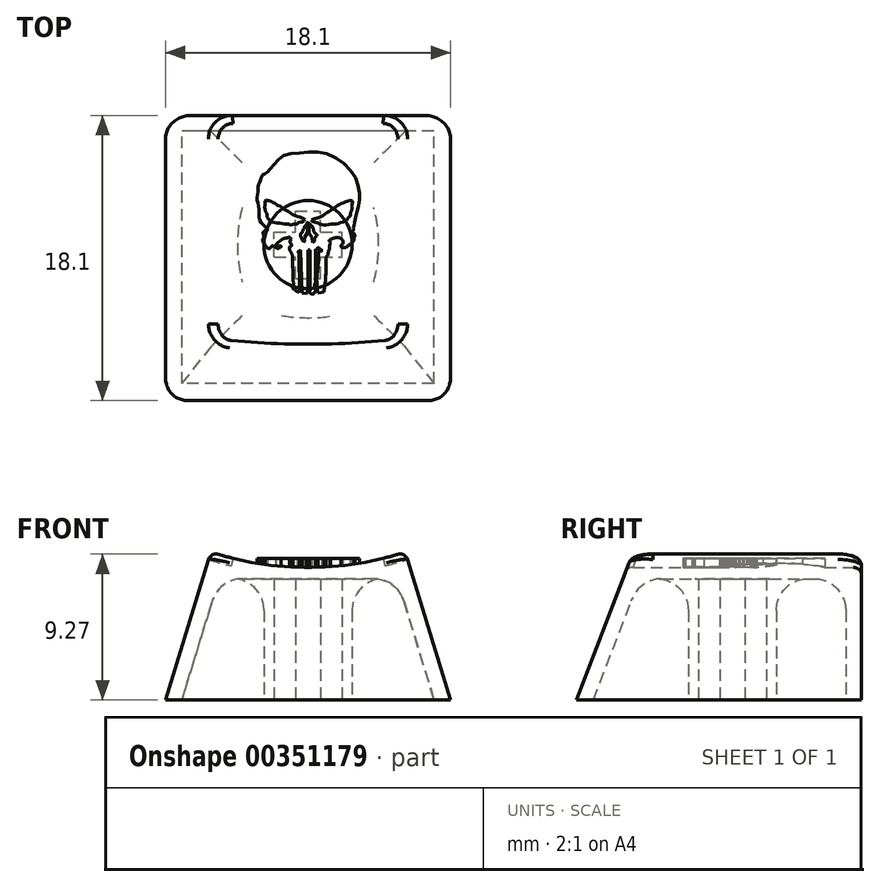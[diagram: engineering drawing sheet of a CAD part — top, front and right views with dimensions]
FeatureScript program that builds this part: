
annotation { "Feature Type Name" : "Feature", "Feature Type Description" : "" }
export const myFeature = defineFeature(function(context is Context, id is Id, definition is map)
    precondition{}
    {
        {
            var Q0;
            Q0=qCreatedBy(makeId("Front.planeOp"),FACE);
            var sketch = newSketch(context, id + "F0", { "sketchPlane" : qUnion([Q0])});
            skLineSegment(sketch, "E0", {"start": v(-8, 0) * mm, "end": v(-5.66, 7.7) * mm});
            skLineSegment(sketch, "E1", {"start": v(-5.66, 7.7) * mm, "end": v(5.66, 7.7) * mm});
            skLineSegment(sketch, "E2", {"start": v(5.66, 7.7) * mm, "end": v(8, 0) * mm});
            skLineSegment(sketch, "E3", {"start": v(8, 0) * mm, "end": v(9.05, 0) * mm});
            skLineSegment(sketch, "E4", {"start": v(9.05, 0) * mm, "end": v(6.18, 9.4) * mm});
            skLineSegment(sketch, "E5", {"start": v(-6.19, 9.4) * mm, "end": v(-9.05, 0) * mm});
            skLineSegment(sketch, "E6", {"start": v(-9.05, 0) * mm, "end": v(-8, 0) * mm});
            skArc(sketch, "E7", {"start": v(-6.18, 9.4) * mm, "mid": v(0, 8.42) * mm, "end": v(6.18, 9.4) * mm});
            skSolve(sketch);
        }
        {
            var Q0;
            Q0 = qSketchRegion(id + "F0", true);
            extrude(context, id + "F1", {"entities" : qUnion([Q0]), "depth" : 4.2 * mm, "hasSecondDirection" : true, "secondDirectionOppositeDirection" : true, "secondDirectionDepth" : 8.2 * mm});
        }
        {
            var Q0;
            Q0=qCreatedBy(makeId("Right.planeOp"),FACE);
            var sketch = newSketch(context, id + "F2", { "sketchPlane" : qUnion([Q0])});
            skLineSegment(sketch, "E8.0.0", {"start": v(8.2, 0) * mm, "end": v(8.2, 7.7) * mm});
            skLineSegment(sketch, "E8.0.1", {"start": v(8.2, 7.7) * mm, "end": v(-4.2, 7.7) * mm});
            skLineSegment(sketch, "E8.0.2", {"start": v(-4.2, 7.7) * mm, "end": v(-4.2, 0) * mm});
            skLineSegment(sketch, "E8.0.3", {"start": v(-4.2, 0) * mm, "end": v(8.2, 0) * mm});
            skLineSegment(sketch, "E9", {"start": v(7.2, 7.7) * mm, "end": v(7.2, 0) * mm});
            skLineSegment(sketch, "E10", {"start": v(7.2, 0) * mm, "end": v(8.2, 0) * mm});
            skLineSegment(sketch, "E11", {"start": v(-6.67, 8.42) * mm, "end": v(-9.9, 0) * mm});
            skLineSegment(sketch, "E12", {"start": v(-9.9, 0) * mm, "end": v(-8.83, 0) * mm});
            skLineSegment(sketch, "E13", {"start": v(-8.83, 0) * mm, "end": v(-5.87, 7.7) * mm});
            skLineSegment(sketch, "E14", {"start": v(-4.2, 7.7) * mm, "end": v(-5.87, 7.7) * mm});
            skLineSegment(sketch, "E15", {"start": v(-4.2, 9.4) * mm, "end": v(-4.2, 7.7) * mm});
            skLineSegment(sketch, "E16.0.0", {"start": v(-4.2, 9.4) * mm, "end": v(-4.2, 8.42) * mm});
            skLineSegment(sketch, "E16.0.1", {"start": v(-4.2, 9.4) * mm, "end": v(-4.2, 0) * mm});
            skLineSegment(sketch, "E16.0.3", {"start": v(-4.2, 0) * mm, "end": v(-4.2, 7.7) * mm});
            skLineSegment(sketch, "E16.0.7", {"start": v(-4.2, 0) * mm, "end": v(-4.2, 9.4) * mm});
            skLineSegment(sketch, "E17", {"start": v(8.2, 8.42) * mm, "end": v(-4.2, 8.42) * mm});
            skLineSegment(sketch, "E18", {"start": v(-4.2, 8.42) * mm, "end": v(-6.67, 8.42) * mm});
            skSolve(sketch);
        }
        {
            var Q0;
            Q0=makeQuery(id+"F2.imprint","IMPRINT",FACE,{"disambiguationData":[TD([[makeQuery(id+"F2.imprint","IMPRINT",EDGE,{"derivedFrom":sQuery(id+"F2.wireOp",EDGE,"E11")}),1.0]])]});
            var Q1;
            {var subQ0=sQuery(id+"F2.wireOp",EDGE,"E14");Q1=makeQuery(id+"F2.imprint","IMPRINT",FACE,{"disambiguationData":[TD([[makeQuery(id+"F2.imprint","IMPRINT",EDGE,{"derivedFrom":subQ0}),1.0]])]});}
            var Q2;
            {var subQ0=sQuery(id+"F2.wireOp",EDGE,"E8.0.0");Q2=makeQuery(id+"F2.imprint","IMPRINT",FACE,{"disambiguationData":[TD([[makeQuery(id+"F2.imprint","IMPRINT",EDGE,{"derivedFrom":subQ0}),1.0]])]});}
            var Q3;
            Q3=makeQuery(id+"F1.opExtrude","SWEPT_FACE",FACE,{"disambiguationData":[OSD([sQuery(id+"F0.wireOp",EDGE,"E4")])]});
            var Q4;
            Q4=makeQuery(id+"F1.opExtrude","SWEPT_FACE",FACE,{"disambiguationData":[OSD([sQuery(id+"F0.wireOp",EDGE,"E5")])]});
            extrude(context, id + "F3", {"entities" : qUnion([Q0, Q1, Q2]), "operationType" : NewBodyOperationType.ADD, "endBound" : BoundingType.UP_TO_SURFACE, "endBoundEntityFace" : qUnion([Q3]), "depth" : 25 * mm, "hasSecondDirection" : true, "secondDirectionBound" : SecondDirectionBoundingType.UP_TO_SURFACE, "secondDirectionOppositeDirection" : true, "secondDirectionBoundEntityFace" : qUnion([Q4]), "secondDirectionDepth" : 25 * mm});
        }
        {
            var Q0;
            {var subQ0=sQuery(id+"F0.wireOp",EDGE,"E4");var subQ1=makeQuery(id+"F1.opExtrude","SWEPT_FACE",FACE,{"disambiguationData":[OSD([subQ0])]});var subQ2=sQuery(id+"F0.wireOp",EDGE,"E3");var subQ3=sQuery(id+"F0.wireOp",EDGE,"E2");var subQ4=sQuery(id+"F0.wireOp",EDGE,"E1");var subQ5=sQuery(id+"F2.wireOp",EDGE,"E14");var subQ6=sQuery(id+"F0.wireOp",EDGE,"E6");Q0=makeQuery(id+"F3.boolean.opBoolean","SPLIT",FACE,{"disambiguationData":[TD([makeQuery(id+"F1.opExtrude","SWEPT_FACE",FACE,{"disambiguationData":[OSD([subQ4])]}),makeQuery(id+"F1.opExtrude","SWEPT_FACE",FACE,{"disambiguationData":[OSD([subQ3])]}),makeQuery(id+"F1.opExtrude","SWEPT_FACE",FACE,{"disambiguationData":[OSD([subQ2])]}),subQ1,makeQuery(id+"F1.opExtrude","SWEPT_FACE",FACE,{"disambiguationData":[OSD([subQ6])]}),makeQuery(id+"F3.opExtrude","SWEPT_FACE",FACE,{"disambiguationData":[OSD([sQuery(id+"F2.wireOp",EDGE,"E10")])]}),makeQuery(id+"F3.opExtrude","SWEPT_FACE",FACE,{"disambiguationData":[OSD([subQ5])]}),makeQuery(id+"F3.opExtrude","CAP_FACE",FACE,{"disambiguationData":[OSD([sQuery(id+"F2.wireOp",EDGE,"E11"),sQuery(id+"F2.wireOp",EDGE,"E12"),sQuery(id+"F2.wireOp",EDGE,"E13"),subQ5,sQuery(id+"F2.wireOp",EDGE,"E16.0.7"),sQuery(id+"F2.wireOp",EDGE,"E18")]),topologyDisambiguationEdgeConnected([subQ1])],"isStart":false})])],"derivedFrom":makeQuery(id+"F1.opExtrude","CAP_FACE",FACE,{"disambiguationData":[OSD([sQuery(id+"F0.wireOp",EDGE,"E0"),subQ4,subQ3,subQ2,subQ0,sQuery(id+"F0.wireOp",EDGE,"E5"),subQ6,sQuery(id+"F0.wireOp",EDGE,"E7")])],"isStart":false})});}
            var Q1;
            {var subQ0=sQuery(id+"F0.wireOp",EDGE,"E5");var subQ1=makeQuery(id+"F1.opExtrude","SWEPT_FACE",FACE,{"disambiguationData":[OSD([subQ0])]});var subQ2=sQuery(id+"F0.wireOp",EDGE,"E1");var subQ3=sQuery(id+"F0.wireOp",EDGE,"E3");var subQ4=sQuery(id+"F0.wireOp",EDGE,"E0");var subQ5=sQuery(id+"F0.wireOp",EDGE,"E6");var subQ6=sQuery(id+"F2.wireOp",EDGE,"E14");Q1=makeQuery(id+"F3.boolean.opBoolean","SPLIT",FACE,{"disambiguationData":[TD([makeQuery(id+"F1.opExtrude","SWEPT_FACE",FACE,{"disambiguationData":[OSD([subQ4])]}),makeQuery(id+"F1.opExtrude","SWEPT_FACE",FACE,{"disambiguationData":[OSD([subQ2])]}),makeQuery(id+"F1.opExtrude","SWEPT_FACE",FACE,{"disambiguationData":[OSD([subQ3])]}),subQ1,makeQuery(id+"F1.opExtrude","SWEPT_FACE",FACE,{"disambiguationData":[OSD([subQ5])]}),makeQuery(id+"F3.opExtrude","SWEPT_FACE",FACE,{"disambiguationData":[OSD([sQuery(id+"F2.wireOp",EDGE,"E10")])]}),makeQuery(id+"F3.opExtrude","SWEPT_FACE",FACE,{"disambiguationData":[OSD([subQ6])]}),makeQuery(id+"F3.opExtrude","CAP_FACE",FACE,{"disambiguationData":[OSD([sQuery(id+"F2.wireOp",EDGE,"E11"),sQuery(id+"F2.wireOp",EDGE,"E12"),sQuery(id+"F2.wireOp",EDGE,"E13"),subQ6,sQuery(id+"F2.wireOp",EDGE,"E16.0.7"),sQuery(id+"F2.wireOp",EDGE,"E18")]),topologyDisambiguationEdgeConnected([subQ1])],"isStart":false})])],"derivedFrom":makeQuery(id+"F1.opExtrude","CAP_FACE",FACE,{"disambiguationData":[OSD([subQ4,subQ2,sQuery(id+"F0.wireOp",EDGE,"E2"),subQ3,sQuery(id+"F0.wireOp",EDGE,"E4"),subQ0,subQ5,sQuery(id+"F0.wireOp",EDGE,"E7")])],"isStart":false})});}
            var Q2;
            Q2=makeQuery(id+"F3.opExtrude","SWEPT_FACE",FACE,{"disambiguationData":[OSD([sQuery(id+"F2.wireOp",EDGE,"E13")])]});
            extrude(context, id + "F4", {"entities" : qUnion([Q0, Q1]), "operationType" : NewBodyOperationType.ADD, "endBound" : BoundingType.UP_TO_SURFACE, "endBoundEntityFace" : qUnion([Q2]), "depth" : 25 * mm});
        }
        {
            var Q0;
            {var subQ0=sQuery(id+"F0.wireOp",EDGE,"E7");var subQ1=sQuery(id+"F0.wireOp",EDGE,"E4");var subQ2=makeQuery(id+"F1.opExtrude","SWEPT_FACE",FACE,{"disambiguationData":[OSD([subQ1])]});var subQ3=sQuery(id+"F2.wireOp",EDGE,"E18");var subQ4=makeQuery(id+"F1.opExtrude","CAP_FACE",FACE,{"disambiguationData":[OSD([sQuery(id+"F0.wireOp",EDGE,"E0"),sQuery(id+"F0.wireOp",EDGE,"E1"),sQuery(id+"F0.wireOp",EDGE,"E2"),sQuery(id+"F0.wireOp",EDGE,"E3"),subQ1,sQuery(id+"F0.wireOp",EDGE,"E5"),sQuery(id+"F0.wireOp",EDGE,"E6"),subQ0])],"isStart":false});Q0=makeQuery(id+"F3.boolean.opBoolean","SPLIT",FACE,{"disambiguationData":[TD([subQ4,subQ2,makeQuery(id+"F1.opExtrude","SWEPT_FACE",FACE,{"disambiguationData":[OSD([subQ0])]}),makeQuery(id+"F3.opExtrude","SWEPT_FACE",FACE,{"disambiguationData":[OSD([subQ3])]}),makeQuery(id+"F3.opExtrude","CAP_FACE",FACE,{"disambiguationData":[OSD([sQuery(id+"F2.wireOp",EDGE,"E11"),sQuery(id+"F2.wireOp",EDGE,"E12"),sQuery(id+"F2.wireOp",EDGE,"E13"),sQuery(id+"F2.wireOp",EDGE,"E14"),sQuery(id+"F2.wireOp",EDGE,"E16.0.7"),subQ3]),topologyDisambiguationEdgeConnected([subQ2])],"isStart":false})])],"derivedFrom":subQ4});}
            var Q1;
            {var subQ0=sQuery(id+"F0.wireOp",EDGE,"E7");var subQ1=sQuery(id+"F2.wireOp",EDGE,"E18");var subQ2=sQuery(id+"F0.wireOp",EDGE,"E5");var subQ3=makeQuery(id+"F1.opExtrude","SWEPT_FACE",FACE,{"disambiguationData":[OSD([subQ2])]});var subQ4=makeQuery(id+"F1.opExtrude","CAP_FACE",FACE,{"disambiguationData":[OSD([sQuery(id+"F0.wireOp",EDGE,"E0"),sQuery(id+"F0.wireOp",EDGE,"E1"),sQuery(id+"F0.wireOp",EDGE,"E2"),sQuery(id+"F0.wireOp",EDGE,"E3"),sQuery(id+"F0.wireOp",EDGE,"E4"),subQ2,sQuery(id+"F0.wireOp",EDGE,"E6"),subQ0])],"isStart":false});Q1=makeQuery(id+"F3.boolean.opBoolean","SPLIT",FACE,{"disambiguationData":[TD([subQ4,subQ3,makeQuery(id+"F1.opExtrude","SWEPT_FACE",FACE,{"disambiguationData":[OSD([subQ0])]}),makeQuery(id+"F3.opExtrude","SWEPT_FACE",FACE,{"disambiguationData":[OSD([subQ1])]}),makeQuery(id+"F3.opExtrude","CAP_FACE",FACE,{"disambiguationData":[OSD([sQuery(id+"F2.wireOp",EDGE,"E11"),sQuery(id+"F2.wireOp",EDGE,"E12"),sQuery(id+"F2.wireOp",EDGE,"E13"),sQuery(id+"F2.wireOp",EDGE,"E14"),sQuery(id+"F2.wireOp",EDGE,"E16.0.7"),subQ1]),topologyDisambiguationEdgeConnected([subQ3])],"isStart":false})])],"derivedFrom":subQ4});}
            var Q2;
            Q2=makeQuery(id+"F3.opExtrude","SWEPT_FACE",FACE,{"disambiguationData":[OSD([sQuery(id+"F2.wireOp",EDGE,"E11")])]});
            extrude(context, id + "F5", {"entities" : qUnion([Q0, Q1]), "operationType" : NewBodyOperationType.ADD, "endBound" : BoundingType.UP_TO_SURFACE, "endBoundEntityFace" : qUnion([Q2]), "depth" : 25 * mm});
        }
        {
            var Q0;
            Q0=qCreatedBy(makeId("Top.planeOp"),FACE);
            var sketch = newSketch(context, id + "F6", { "sketchPlane" : qUnion([Q0])});
            skCircle(sketch, "E19", {"center": v(0, 0) * mm, "radius": 2.8 * mm});
            skLineSegment(sketch, "E20.bottom", {"start": v(-2.15, -0.8) * mm, "end": v(-0.8, -0.8) * mm});
            skLineSegment(sketch, "E20.top", {"start": v(-2.15, 0.8) * mm, "end": v(-0.8, 0.8) * mm});
            skLineSegment(sketch, "E20.left", {"start": v(-2.15, -0.8) * mm, "end": v(-2.15, 0.8) * mm});
            skLineSegment(sketch, "E20.right", {"start": v(2.15, -0.8) * mm, "end": v(2.15, 0.8) * mm});
            skLineSegment(sketch, "E21.bottom", {"start": v(-0.8, -2.15) * mm, "end": v(0.8, -2.15) * mm});
            skLineSegment(sketch, "E21.top", {"start": v(-0.8, 2.15) * mm, "end": v(0.8, 2.15) * mm});
            skLineSegment(sketch, "E21.right", {"start": v(0.8, -2.15) * mm, "end": v(0.8, -0.8) * mm});
            skLineSegment(sketch, "E22.trimOffspring", {"start": v(0.8, 0.8) * mm, "end": v(0.8, 2.15) * mm});
            skLineSegment(sketch, "E23.trimOffspring", {"start": v(0.8, -0.8) * mm, "end": v(2.15, -0.8) * mm});
            skLineSegment(sketch, "E24.trimOffspring", {"start": v(-0.8, 0.8) * mm, "end": v(-0.8, 2.15) * mm});
            skLineSegment(sketch, "E25.trimOffspring", {"start": v(0.8, 0.8) * mm, "end": v(2.15, 0.8) * mm});
            skLineSegment(sketch, "E26", {"start": v(-0.8, -2.15) * mm, "end": v(-0.8, -0.8) * mm});
            skSolve(sketch);
        }
        {
            var Q0;
            Q0=makeQuery(id+"F6.imprint","IMPRINT",FACE,{"disambiguationData":[TD([[makeQuery(id+"F6.imprint","IMPRINT",EDGE,{"derivedFrom":sQuery(id+"F6.wireOp",EDGE,"E19")}),1.0]])]});
            var Q1;
            Q1=makeQuery(id+"F1.opExtrude","SWEPT_FACE",FACE,{"disambiguationData":[OSD([sQuery(id+"F0.wireOp",EDGE,"E1")])]});
            extrude(context, id + "F7", {"entities" : qUnion([Q0]), "operationType" : NewBodyOperationType.ADD, "endBound" : BoundingType.UP_TO_SURFACE, "endBoundEntityFace" : qUnion([Q1]), "depth" : 25 * mm});
        }
        {
            var Q0;
            {var subQ0=sQuery(id+"F0.wireOp",EDGE,"E4");var subQ1=sQuery(id+"F2.wireOp",EDGE,"E11");Q0=makeQuery(id+"F5.boolean.opBoolean","MERGE",EDGE,{"derivedFrom":[makeQuery(id+"F3.opExtrude","CAP_EDGE",EDGE,{"disambiguationData":[OSD([subQ1]),topologyDisambiguationEdgeConnected([makeQuery(id+"F1.opExtrude","SWEPT_FACE",FACE,{"disambiguationData":[OSD([subQ0])]})])],"isStart":false}),makeQuery(id+"F5.opExtrude","CAP_EDGE",EDGE,{"disambiguationData":[OSD([subQ0])],"isStart":false})]});}
            var Q1;
            {var subQ0=sQuery(id+"F0.wireOp",EDGE,"E5");var subQ1=sQuery(id+"F2.wireOp",EDGE,"E11");Q1=makeQuery(id+"F5.boolean.opBoolean","MERGE",EDGE,{"derivedFrom":[makeQuery(id+"F3.opExtrude","CAP_EDGE",EDGE,{"disambiguationData":[OSD([subQ1]),topologyDisambiguationEdgeConnected([makeQuery(id+"F1.opExtrude","SWEPT_FACE",FACE,{"disambiguationData":[OSD([subQ0])]})])],"isStart":false}),makeQuery(id+"F5.opExtrude","CAP_EDGE",EDGE,{"disambiguationData":[OSD([subQ0])],"isStart":false})]});}
            var Q2;
            Q2=makeQuery(id+"F1.opExtrude","CAP_EDGE",EDGE,{"disambiguationData":[OSD([sQuery(id+"F0.wireOp",EDGE,"E4")])],"isStart":true});
            var Q3;
            Q3=makeQuery(id+"F1.opExtrude","CAP_EDGE",EDGE,{"disambiguationData":[OSD([sQuery(id+"F0.wireOp",EDGE,"E5")])],"isStart":true});
            fillet(context, id + "F8", {"entities" : qUnion([Q0, Q1, Q2, Q3]), "radius" : 1.5 * mm, "tangentPropagation" : true, "allowEdgeOverflow" : false});
        }
        {
            var Q0;
            {var subQ0=sQuery(id+"F0.wireOp",EDGE,"E7");var subQ1=sQuery(id+"F0.wireOp",EDGE,"E5");Q0=makeQuery(id+"F5.boolean.opBoolean","MERGE",EDGE,{"derivedFrom":[makeQuery(id+"F1.opExtrude","SWEPT_EDGE",EDGE,{"disambiguationData":[OSD([subQ1,subQ0])]}),makeQuery(id+"F5.opExtrude","SWEPT_EDGE",EDGE,{"disambiguationData":[OSD([subQ1,subQ0])]})]});}
            fillet(context, id + "F9", {"entities" : qUnion([Q0]), "radius" : 0.5 * mm, "tangentPropagation" : true, "allowEdgeOverflow" : false});
        }
        {
            var Q0;
            {var subQ1=sQuery(id+"F0.wireOp",EDGE,"E0");Q0=makeQuery(id+"F7.boolean.opBoolean","SPLIT",FACE,{"disambiguationData":[TD([makeQuery(id+"F1.opExtrude","SWEPT_FACE",FACE,{"disambiguationData":[OSD([subQ1])]})])],"derivedFrom":makeQuery(id+"F3.boolean.opBoolean","MERGE",FACE,{"derivedFrom":[makeQuery(id+"F1.opExtrude","SWEPT_FACE",FACE,{"disambiguationData":[OSD([sQuery(id+"F0.wireOp",EDGE,"E1")])]}),makeQuery(id+"F3.opExtrude","SWEPT_FACE",FACE,{"disambiguationData":[OSD([sQuery(id+"F2.wireOp",EDGE,"E14")])]})]})});}
            fillet(context, id + "F10", {"entities" : qUnion([Q0]), "radius" : 2 * mm, "tangentPropagation" : true, "allowEdgeOverflow" : false});
        }
        {
            var Q0;
            Q0=qCreatedBy(makeId("Top.planeOp"),FACE);
            cPlane(context, id + "F11", {"entities" : qUnion([Q0]), "cplaneType" : CPlaneType.OFFSET, "offset" : 9 * mm, "width" : 150 * mm, "height" : 150 * mm});
        }
        {
            var Q0;
            Q0=qCreatedBy(id+"F11.planeOp",FACE);
            var sketch = newSketch(context, id + "F12", { "sketchPlane" : qUnion([Q0])});
            skFitSpline(sketch, "E27.0.0", {"points": [v(1, -3.01) * mm, v(1.09, -2.41) * mm, v(1.13, -1.8) * mm]});
            skLineSegment(sketch, "E27.0.1", {"start": v(1.13, -1.8) * mm, "end": v(1.13, -0.78) * mm});
            skFitSpline(sketch, "E27.0.2", {"points": [v(1.36, 0.27) * mm, v(1.34, 0.25) * mm, v(1.37, 0.22) * mm, v(1.42, 0.12) * mm, v(1.38, -0.04) * mm, v(1.38, -0.24) * mm, v(1.28, -0.5) * mm, v(1.24, -0.7) * mm, v(1.13, -0.78) * mm]});
            skFitSpline(sketch, "E27.0.3", {"points": [v(2.12, -0.01) * mm, v(2.14, 0.01) * mm, v(2.18, 0.04) * mm, v(2.21, 0.1) * mm, v(2.22, 0.15) * mm, v(2.22, 0.2) * mm, v(2.2, 0.27) * mm, v(2.18, 0.33) * mm, v(2.13, 0.37) * mm, v(2.07, 0.4) * mm, v(2, 0.44) * mm, v(1.93, 0.46) * mm, v(1.85, 0.46) * mm, v(1.77, 0.46) * mm, v(1.7, 0.42) * mm, v(1.6, 0.4) * mm, v(1.48, 0.35) * mm, v(1.38, 0.32) * mm, v(1.36, 0.27) * mm]});
            skFitSpline(sketch, "E27.0.4", {"points": [v(2.93, 0.42) * mm, v(2.92, 0.36) * mm, v(2.92, 0.27) * mm, v(2.84, 0.19) * mm, v(2.8, 0.11) * mm, v(2.71, 0.06) * mm, v(2.62, 0) * mm, v(2.52, -0.09) * mm, v(2.43, -0.17) * mm, v(2.33, -0.2) * mm, v(2.25, -0.18) * mm, v(2.13, -0.16) * mm, v(2.1, -0.06) * mm, v(2.12, -0.01) * mm]});
            skFitSpline(sketch, "E27.0.5", {"points": [v(2.83, 0.76) * mm, v(2.85, 0.74) * mm, v(2.9, 0.73) * mm, v(2.96, 0.65) * mm, v(2.97, 0.54) * mm, v(2.93, 0.46) * mm, v(2.93, 0.42) * mm]});
            skFitSpline(sketch, "E27.0.6", {"points": [v(2.87, 1.04) * mm, v(2.88, 1) * mm, v(2.89, 0.93) * mm, v(2.83, 0.85) * mm, v(2.82, 0.79) * mm, v(2.83, 0.76) * mm]});
            skFitSpline(sketch, "E27.0.7", {"points": [v(-2.76, 4.5) * mm, v(-2.58, 4.58) * mm, v(-2.36, 4.83) * mm, v(-2.03, 5.23) * mm, v(-1.48, 5.68) * mm, v(-0.4, 5.83) * mm, v(0.9, 5.85) * mm, v(2.27, 5.16) * mm, v(3.06, 4.15) * mm, v(3.26, 3.22) * mm, v(3.22, 2.55) * mm, v(3.1, 2) * mm, v(2.97, 1.5) * mm, v(2.92, 1.26) * mm, v(2.88, 1.12) * mm, v(2.87, 1.04) * mm]});
            skFitSpline(sketch, "E27.0.8", {"points": [v(-2.57, 0.97) * mm, v(-2.73, 1.16) * mm, v(-3.06, 1.52) * mm, v(-3.12, 2.3) * mm, v(-3.23, 2.9) * mm, v(-3.18, 3.4) * mm, v(-3.17, 3.75) * mm, v(-3, 4.1) * mm, v(-2.92, 4.38) * mm, v(-2.76, 4.5) * mm]});
            skFitSpline(sketch, "E27.0.9", {"points": [v(-2.84, 0.74) * mm, v(-2.85, 0.8) * mm, v(-2.8, 0.85) * mm, v(-2.71, 0.9) * mm, v(-2.63, 0.9) * mm, v(-2.56, 0.93) * mm, v(-2.57, 0.97) * mm]});
            skFitSpline(sketch, "E27.0.10", {"points": [v(-2.73, 0) * mm, v(-2.8, 0.08) * mm, v(-2.86, 0.2) * mm, v(-2.88, 0.34) * mm, v(-2.85, 0.4) * mm, v(-2.82, 0.42) * mm, v(-2.78, 0.44) * mm, v(-2.76, 0.48) * mm, v(-2.8, 0.52) * mm, v(-2.83, 0.61) * mm, v(-2.84, 0.69) * mm, v(-2.84, 0.74) * mm]});
            skFitSpline(sketch, "E27.0.11", {"points": [v(-1.72, -0.12) * mm, v(-1.73, -0.18) * mm, v(-1.8, -0.19) * mm, v(-1.86, -0.23) * mm, v(-1.91, -0.25) * mm, v(-2, -0.2) * mm, v(-2.09, -0.14) * mm, v(-2.17, -0.1) * mm, v(-2.22, -0.07) * mm, v(-2.27, -0.09) * mm, v(-2.32, -0.13) * mm, v(-2.37, -0.17) * mm, v(-2.44, -0.24) * mm, v(-2.55, -0.24) * mm, v(-2.63, -0.17) * mm, v(-2.68, -0.1) * mm, v(-2.7, -0.03) * mm, v(-2.73, 0) * mm]});
            skFitSpline(sketch, "E27.0.12", {"points": [v(-1.98, 0.04) * mm, v(-2, 0.02) * mm, v(-2.04, 0.02) * mm, v(-2.05, -0.04) * mm, v(-2, -0.06) * mm, v(-1.96, -0.07) * mm, v(-1.9, -0.09) * mm, v(-1.85, -0.07) * mm, v(-1.78, -0.09) * mm, v(-1.72, -0.08) * mm, v(-1.72, -0.12) * mm]});
            skFitSpline(sketch, "E27.0.13", {"points": [v(-1.15, -0.1) * mm, v(-1.13, -0.1) * mm, v(-1.03, -0.09) * mm, v(-1.07, 0) * mm, v(-1.1, 0.08) * mm, v(-1.15, 0.17) * mm, v(-1.14, 0.26) * mm, v(-1.1, 0.3) * mm, v(-1.06, 0.33) * mm, v(-1.08, 0.39) * mm, v(-1.13, 0.42) * mm, v(-1.19, 0.47) * mm, v(-1.28, 0.45) * mm, v(-1.4, 0.43) * mm, v(-1.55, 0.4) * mm, v(-1.75, 0.25) * mm, v(-1.9, 0.13) * mm, v(-1.98, 0.04) * mm]});
            skFitSpline(sketch, "E27.0.14", {"points": [v(-1, -0.7) * mm, v(-1.06, -0.5) * mm, v(-1.17, -0.31) * mm, v(-1.15, -0.1) * mm]});
            skLineSegment(sketch, "E27.0.15", {"start": v(-1, -0.7) * mm, "end": v(-0.95, -2.34) * mm});
            skFitSpline(sketch, "E27.0.16", {"points": [v(-0.54, -2.95) * mm, v(-0.56, -2.97) * mm, v(-0.63, -3.01) * mm, v(-0.75, -2.94) * mm, v(-0.85, -2.88) * mm, v(-1, -2.68) * mm, v(-0.9, -2.47) * mm, v(-0.95, -2.34) * mm]});
            skLineSegment(sketch, "E27.0.17", {"start": v(-0.54, -2.95) * mm, "end": v(-0.58, -0.57) * mm});
            skFitSpline(sketch, "E27.0.18", {"points": [v(-0.58, -0.57) * mm, v(-0.6, -0.5) * mm, v(-0.65, -0.44) * mm]});
            skFitSpline(sketch, "E27.0.19", {"points": [v(-0.65, -0.44) * mm, v(-0.58, -0.42) * mm, v(-0.52, -0.38) * mm, v(-0.47, -0.33) * mm]});
            skLineSegment(sketch, "E27.0.20", {"start": v(-0.47, -0.33) * mm, "end": v(-0.38, -3.06) * mm});
            skLineSegment(sketch, "E27.0.21", {"start": v(-0.38, -3.06) * mm, "end": v(-0.08, -3.1) * mm});
            skFitSpline(sketch, "E27.0.22", {"points": [v(-0.08, -3.1) * mm, v(0, -2.81) * mm, v(0, -2.52) * mm]});
            skLineSegment(sketch, "E27.0.23", {"start": v(0, -2.52) * mm, "end": v(0, -0.34) * mm});
            skLineSegment(sketch, "E27.0.24", {"start": v(0, -0.34) * mm, "end": v(0.11, -0.34) * mm});
            skLineSegment(sketch, "E27.0.25", {"start": v(0.11, -0.34) * mm, "end": v(0.11, -2.95) * mm});
            skFitSpline(sketch, "E27.0.26", {"points": [v(0.49, -2.42) * mm, v(0.41, -2.61) * mm, v(0.49, -2.85) * mm, v(0.33, -3.13) * mm, v(0.16, -3.1) * mm, v(0.1, -3.02) * mm, v(0.11, -2.95) * mm]});
            skLineSegment(sketch, "E27.0.27", {"start": v(0.49, -2.42) * mm, "end": v(0.49, -0.29) * mm});
            skFitSpline(sketch, "E27.0.28", {"points": [v(0.88, -0.36) * mm, v(0.84, -0.33) * mm, v(0.76, -0.3) * mm, v(0.65, -0.19) * mm, v(0.53, -0.3) * mm, v(0.49, -0.29) * mm]});
            skFitSpline(sketch, "E27.0.29", {"points": [v(0.88, -0.36) * mm, v(0.88, -0.38) * mm, v(0.85, -0.4) * mm, v(0.77, -0.38) * mm, v(0.7, -0.43) * mm, v(0.67, -0.46) * mm]});
            skFitSpline(sketch, "E27.0.30", {"points": [v(0.63, -3.06) * mm, v(0.55, -2.2) * mm, v(0.64, -1.32) * mm, v(0.67, -0.46) * mm]});
            skLineSegment(sketch, "E27.0.31", {"start": v(0.63, -3.06) * mm, "end": v(1, -3.01) * mm});
            skFitSpline(sketch, "E28.0", {"points": [v(-0.19, 1.6) * mm, v(-0.2, 1.58) * mm, v(-0.24, 1.52) * mm, v(-0.39, 1.44) * mm, v(-0.57, 1.4) * mm, v(-0.73, 1.3) * mm, v(-0.88, 1.32) * mm, v(-1.03, 1.26) * mm, v(-1.24, 1.3) * mm, v(-1.51, 1.31) * mm, v(-1.85, 1.38) * mm, v(-2.2, 1.41) * mm, v(-2.5, 1.62) * mm, v(-2.61, 1.83) * mm, v(-2.62, 1.97) * mm]});
            skFitSpline(sketch, "E29.0", {"points": [v(0.23, 1.55) * mm, v(0.31, 1.6) * mm, v(0.54, 1.68) * mm, v(0.9, 1.8) * mm, v(1.32, 2.1) * mm, v(1.68, 2.3) * mm, v(1.95, 2.54) * mm, v(2.27, 2.66) * mm, v(2.53, 2.78) * mm, v(2.76, 2.79) * mm]});
            skFitSpline(sketch, "E30.0", {"points": [v(2.68, 1.97) * mm, v(2.7, 2.01) * mm, v(2.74, 2.13) * mm, v(2.8, 2.35) * mm, v(2.8, 2.58) * mm, v(2.83, 2.76) * mm, v(2.76, 2.79) * mm]});
            skFitSpline(sketch, "E31.0", {"points": [v(0.23, 1.55) * mm, v(0.24, 1.5) * mm, v(0.32, 1.46) * mm, v(0.45, 1.43) * mm, v(0.62, 1.37) * mm, v(0.82, 1.28) * mm, v(1.1, 1.24) * mm, v(1.44, 1.3) * mm, v(1.8, 1.31) * mm, v(2.1, 1.4) * mm, v(2.38, 1.48) * mm, v(2.52, 1.66) * mm, v(2.66, 1.8) * mm, v(2.7, 1.9) * mm, v(2.68, 1.97) * mm]});
            skFitSpline(sketch, "E32.0", {"points": [v(0.54, 0.67) * mm, v(0.38, 0.8) * mm, v(0.33, 1) * mm, v(0.27, 1.19) * mm]});
            skFitSpline(sketch, "E33.0", {"points": [v(0.28, 0.15) * mm, v(0.4, 0.22) * mm, v(0.44, 0.42) * mm, v(0.56, 0.59) * mm, v(0.54, 0.67) * mm]});
            skLineSegment(sketch, "E34.0", {"start": v(0.07, 0.75) * mm, "end": v(0.26, 0.45) * mm});
            skLineSegment(sketch, "E35.0", {"start": v(0.26, 0.45) * mm, "end": v(0.28, 0.15) * mm});
            skLineSegment(sketch, "E36.0", {"start": v(0.08, 1.33) * mm, "end": v(0.07, 0.75) * mm});
            skFitSpline(sketch, "E37.0", {"points": [v(0.27, 1.19) * mm, v(0.23, 1.22) * mm, v(0.14, 1.25) * mm, v(0.12, 1.33) * mm, v(0.1, 1.35) * mm, v(0.08, 1.33) * mm]});
            skLineSegment(sketch, "E38.0", {"start": v(-0.02, 1.4) * mm, "end": v(-0.03, 0.77) * mm});
            skFitSpline(sketch, "E39.0", {"points": [v(-0.2, 1.18) * mm, v(-0.19, 1.19) * mm, v(-0.15, 1.21) * mm, v(-0.1, 1.26) * mm, v(-0.06, 1.32) * mm, v(-0.05, 1.38) * mm, v(-0.04, 1.42) * mm, v(-0.02, 1.4) * mm]});
            skFitSpline(sketch, "E40.0", {"points": [v(-0.23, 0.24) * mm, v(-0.23, 0.19) * mm, v(-0.3, 0.23) * mm, v(-0.37, 0.32) * mm, v(-0.42, 0.45) * mm, v(-0.48, 0.57) * mm, v(-0.47, 0.66) * mm, v(-0.44, 0.73) * mm, v(-0.38, 0.77) * mm, v(-0.33, 0.86) * mm, v(-0.3, 0.98) * mm, v(-0.23, 1.08) * mm, v(-0.22, 1.14) * mm, v(-0.22, 1.15) * mm]});
            skArc(sketch, "E41.0", {"start": v(-0.22, 1.15) * mm, "mid": v(-0.21, 1.17) * mm, "end": v(-0.2, 1.18) * mm});
            skLineSegment(sketch, "E42.0", {"start": v(-0.03, 0.77) * mm, "end": v(-0.21, 0.46) * mm});
            skLineSegment(sketch, "E43.0", {"start": v(-0.21, 0.46) * mm, "end": v(-0.23, 0.24) * mm});
            skFitSpline(sketch, "E44.0", {"points": [v(-0.19, 1.6) * mm, v(-0.33, 1.67) * mm, v(-0.65, 1.8) * mm, v(-1.05, 1.96) * mm, v(-1.36, 2.17) * mm, v(-1.6, 2.32) * mm, v(-1.78, 2.46) * mm, v(-1.95, 2.5) * mm, v(-2.04, 2.58) * mm, v(-2.2, 2.66) * mm, v(-2.36, 2.74) * mm, v(-2.52, 2.8) * mm, v(-2.6, 2.82) * mm, v(-2.65, 2.83) * mm]});
            skFitSpline(sketch, "E45.0", {"points": [v(-2.62, 1.97) * mm, v(-2.64, 2) * mm, v(-2.7, 2.12) * mm, v(-2.75, 2.36) * mm, v(-2.73, 2.58) * mm, v(-2.72, 2.78) * mm, v(-2.67, 2.82) * mm, v(-2.65, 2.83) * mm]});
            skSolve(sketch);
        }
        {
            var Q0;
            Q0=makeQuery(id+"F12.imprint","IMPRINT",FACE,{"disambiguationData":[TD([[makeQuery(id+"F12.imprint","IMPRINT",EDGE,{"derivedFrom":sQuery(id+"F12.wireOp",EDGE,"E27.0.0")}),1.0]])]});
            extrude(context, id + "F13", {"entities" : qUnion([Q0]), "operationType" : NewBodyOperationType.ADD, "endBound" : BoundingType.UP_TO_NEXT, "oppositeDirection" : true, "depth" : 25 * mm});
        }
    });
